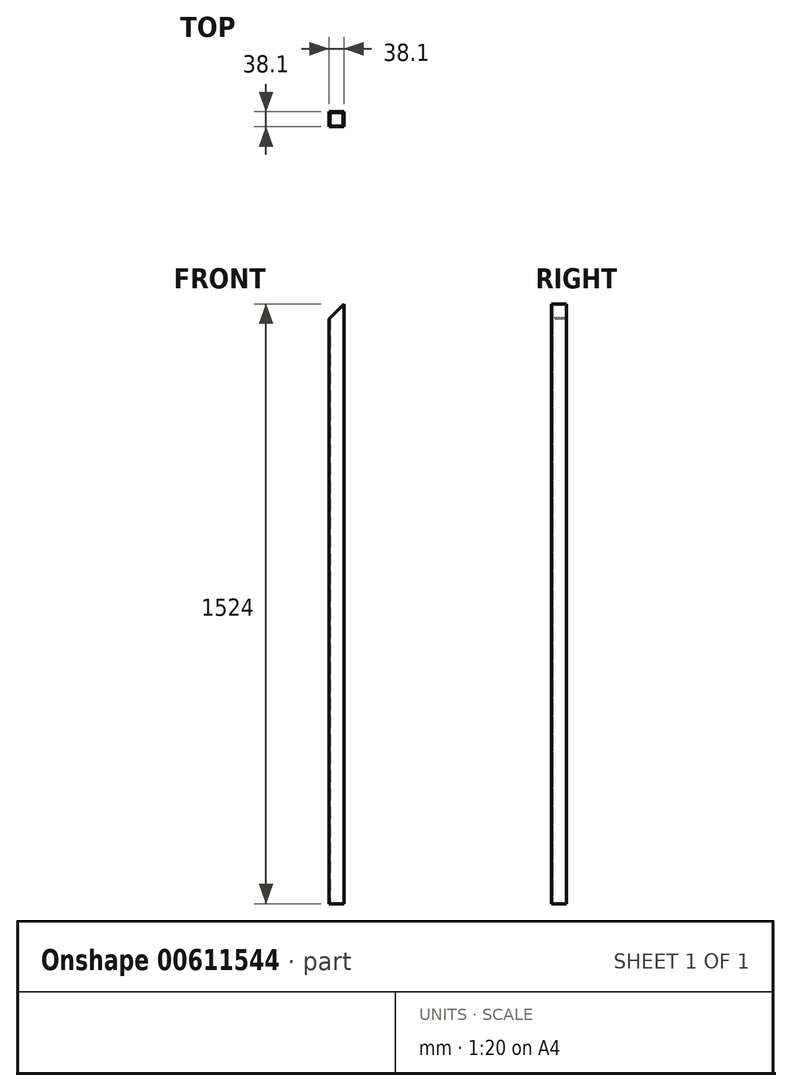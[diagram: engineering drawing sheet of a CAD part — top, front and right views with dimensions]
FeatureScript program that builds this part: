
annotation { "Feature Type Name" : "Feature", "Feature Type Description" : "" }
export const myFeature = defineFeature(function(context is Context, id is Id, definition is map)
    precondition{}
    {
        {
            var Q0;
            Q0=qCreatedBy(makeId("Top.planeOp"),FACE);
            var sketch = newSketch(context, id + "F0", { "sketchPlane" : qUnion([Q0])});
            skLineSegment(sketch, "E0.bottom", {"start": v(0, 0) * mm, "end": v(-38.1, 0) * mm});
            skLineSegment(sketch, "E0.top", {"start": v(0, -38.1) * mm, "end": v(-38.1, -38.1) * mm});
            skLineSegment(sketch, "E0.left", {"start": v(0, 0) * mm, "end": v(0, -38.1) * mm});
            skLineSegment(sketch, "E0.right", {"start": v(-38.1, 0) * mm, "end": v(-38.1, -38.1) * mm});
            skLineSegment(sketch, "E1.bottom", {"start": v(-35.81, -2.29) * mm, "end": v(-2.29, -2.29) * mm});
            skLineSegment(sketch, "E1.top", {"start": v(-35.81, -35.81) * mm, "end": v(-2.29, -35.81) * mm});
            skLineSegment(sketch, "E1.left", {"start": v(-35.81, -2.29) * mm, "end": v(-35.81, -35.81) * mm});
            skLineSegment(sketch, "E1.right", {"start": v(-2.29, -2.29) * mm, "end": v(-2.29, -35.81) * mm});
            skSolve(sketch);
        }
        {
            var Q0;
            Q0 = qSketchRegion(id + "F0", true);
            extrude(context, id + "F1", {"entities" : qUnion([Q0]), "depth" : 1524 * mm, "offsetDistance" : 25.4 * mm});
        }
        {
            var Q0;
            Q0=makeQuery(id+"F1.opExtrude","SWEPT_FACE",FACE,{"disambiguationData":[OSD([sQuery(id+"F0.wireOp",EDGE,"E0.top")])]});
            var sketch = newSketch(context, id + "F2", { "sketchPlane" : qUnion([Q0])});
            skLineSegment(sketch, "E2", {"start": v(0, 1524) * mm, "end": v(-38.1, 1485.9) * mm});
            skLineSegment(sketch, "E3", {"start": v(-38.1, 1485.9) * mm, "end": v(-38.1, 1524) * mm});
            skLineSegment(sketch, "E4", {"start": v(-38.1, 1524) * mm, "end": v(0, 1524) * mm});
            skSolve(sketch);
        }
        {
            var Q0;
            Q0 = qSketchRegion(id + "F2", true);
            extrude(context, id + "F3", {"entities" : qUnion([Q0]), "operationType" : NewBodyOperationType.REMOVE, "oppositeDirection" : true, "depth" : 50.8 * mm, "offsetDistance" : 25.4 * mm});
        }
    });
